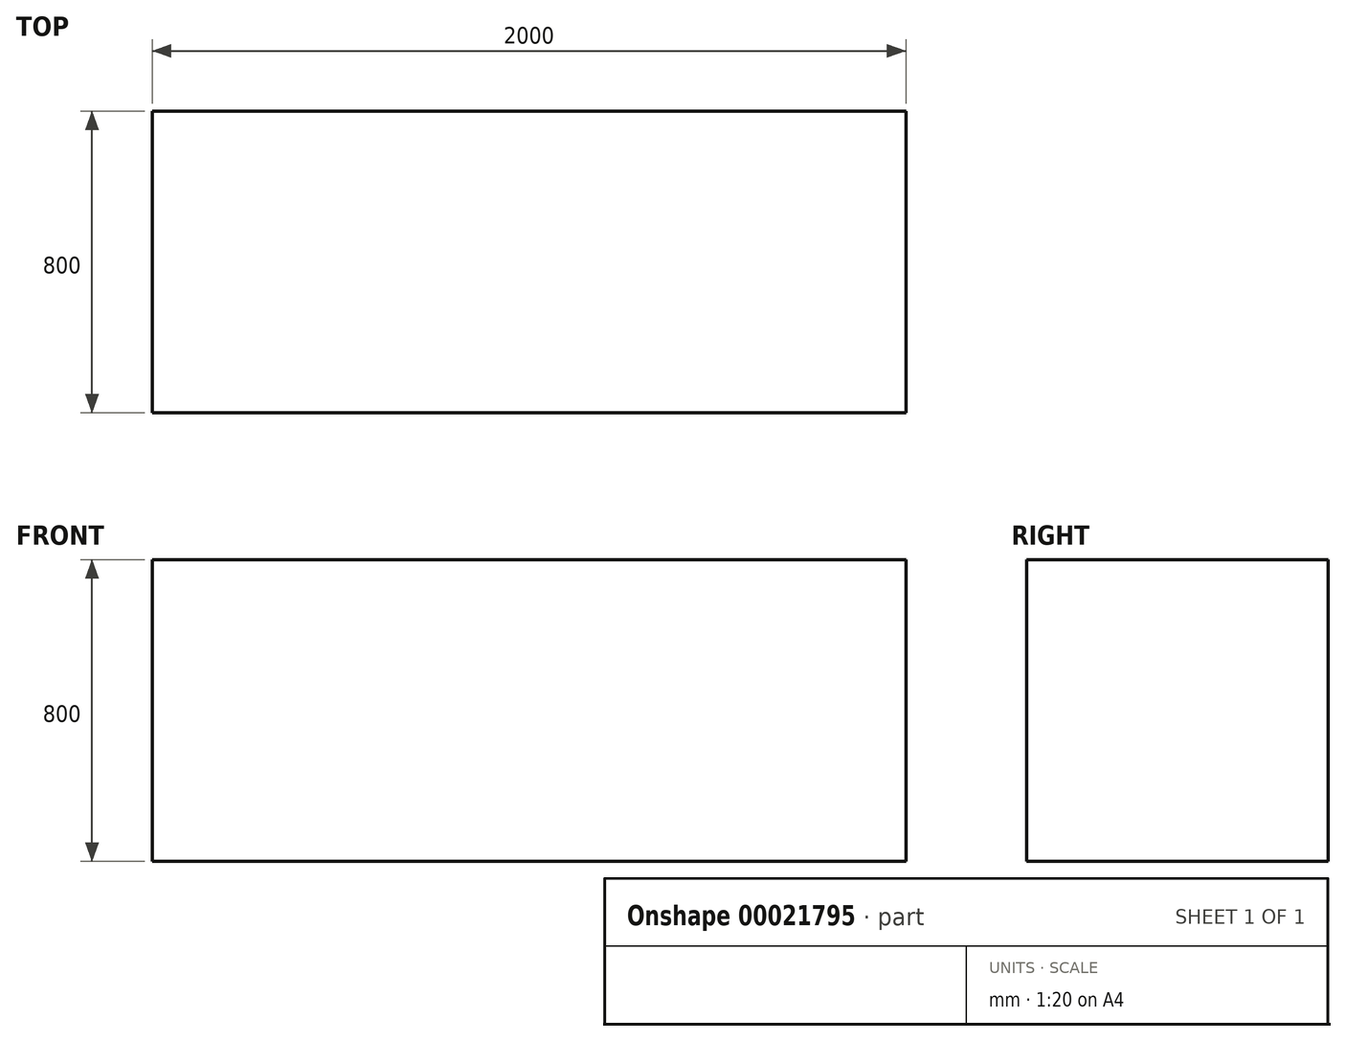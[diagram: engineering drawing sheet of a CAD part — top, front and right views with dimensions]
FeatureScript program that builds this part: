
annotation { "Feature Type Name" : "Feature", "Feature Type Description" : "" }
export const myFeature = defineFeature(function(context is Context, id is Id, definition is map)
    precondition{}
    {
        {
            var Q0;
            Q0=qCreatedBy(makeId("Top.planeOp"),FACE);
            var sketch = newSketch(context, id + "F0", { "sketchPlane" : qUnion([Q0])});
            skLineSegment(sketch, "E0.bottom", {"start": v(0, 0) * mm, "end": v(2000, 0) * mm});
            skLineSegment(sketch, "E0.top", {"start": v(0, 800) * mm, "end": v(2000, 800) * mm});
            skLineSegment(sketch, "E0.left", {"start": v(0, 0) * mm, "end": v(0, 800) * mm});
            skLineSegment(sketch, "E0.right", {"start": v(2000, 0) * mm, "end": v(2000, 800) * mm});
            skSolve(sketch);
        }
        {
            var Q0;
            Q0=makeQuery(id+"F0.imprint","IMPRINT",FACE,{"disambiguationData":[TD([[makeQuery(id+"F0.imprint","IMPRINT",EDGE,{"derivedFrom":sQuery(id+"F0.wireOp",EDGE,"E0.bottom")}),1.0]])]});
            extrude(context, id + "F1", {"entities" : qUnion([Q0]), "depth" : 800 * mm});
        }
    });
